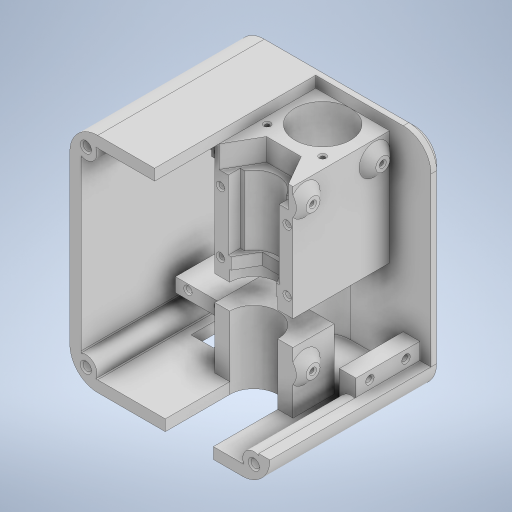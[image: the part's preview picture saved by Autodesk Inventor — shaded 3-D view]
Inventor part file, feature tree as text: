
AUTODESK INVENTOR PART (.ipt)
format: ipt  version: 2023 (Build 270158000, 158)  size: 733,696 bytes
history: native  units: mm
features: sketch x22, extrude x21, projected_geometry x6, chamfer x5, other x3, hole x2, fillet x1
ambient origin geometry x8: Origin, YZ Plane, XZ Plane, XY Plane, X Axis, Y Axis, Z Axis, Center Point
bodies: Body1 (feature_tree)
feature tree (60):
  other  "솔리드1"
  sketch  "스케치1"
  extrude  "돌출1"  Depth=20.0mm
  other  "작업 평면2"
  sketch  "스케치2"
  other  "작업 평면3"
  sketch  "스케치3"
  extrude  "돌출2"  Depth=54.0mm
  extrude  "돌출3"  Depth=40.0mm
  extrude  "돌출4"  Depth=48.0mm
  extrude  "돌출5"  Depth=11.0mm
  extrude  "돌출6"  Depth=2.0mm
  extrude  "돌출8"  Depth=20.0mm
  extrude  "돌출10"  Depth=18.0mm
  hole  "구멍1"  [1 undecoded]
  chamfer  "모따기1"  Distance=13.0mm
  sketch  "스케치12"
  extrude  "돌출14"  Depth=25.0mm
  fillet  "모깎기1"  Radius=13.3mm
  extrude  "돌출15"  Depth=9.95mm
  extrude  "돌출16"  Depth=24.0mm
  extrude  "돌출17"  Depth=16.0mm
  extrude  "돌출18"  Depth=4.5mm
  hole  "구멍2"  [1 undecoded]
  chamfer  "모따기2"  Distance=41.0mm
  sketch  "스케치21"
  extrude  "돌출19"  Depth=5.8mm
  extrude  "돌출20"  TaperAngle=0.0deg  [1 undecoded]
  extrude  "돌출21"  Depth=17.3mm
  extrude  "돌출22"  Depth=18.3mm
  chamfer  "모따기3"  Distance=8.5mm
  extrude  "돌출23"  Depth=8.0mm TaperAngle=0.0deg
  chamfer  "모따기4"  Distance=25.0mm
  extrude  "돌출24"  Depth=16.3mm
  chamfer  "모따기5"  Distance=4.2mm
  extrude  "돌출25"  Depth=17.3mm
  extrude  "돌출26"  Depth=35.0mm TaperAngle=0.0deg
  sketch  "스케치4"
  projected_geometry  "투영된 루프1"
  sketch  "스케치5"
  projected_geometry  "투영된 루프2"
  sketch  "스케치6"
  sketch  "스케치8"
  sketch  "스케치10"
  sketch  "스케치11"
  projected_geometry  "투영된 루프3"
  sketch  "스케치15"
  projected_geometry  "투영된 루프4"
  sketch  "스케치16"
  sketch  "스케치18"
  sketch  "스케치19"
  sketch  "스케치20"
  sketch  "스케치23"
  sketch  "스케치24"
  sketch  "스케치26"
  sketch  "스케치27"
  sketch  "스케치28"
  projected_geometry  "투영된 루프5"
  projected_geometry  "투영된 루프6"
  sketch  "스케치29"
note: 3 required parameter values undecoded (feature->parameter linkage not recoverable at this tier; creation-order binding heuristic only, values carry confidence <= 0.55)
